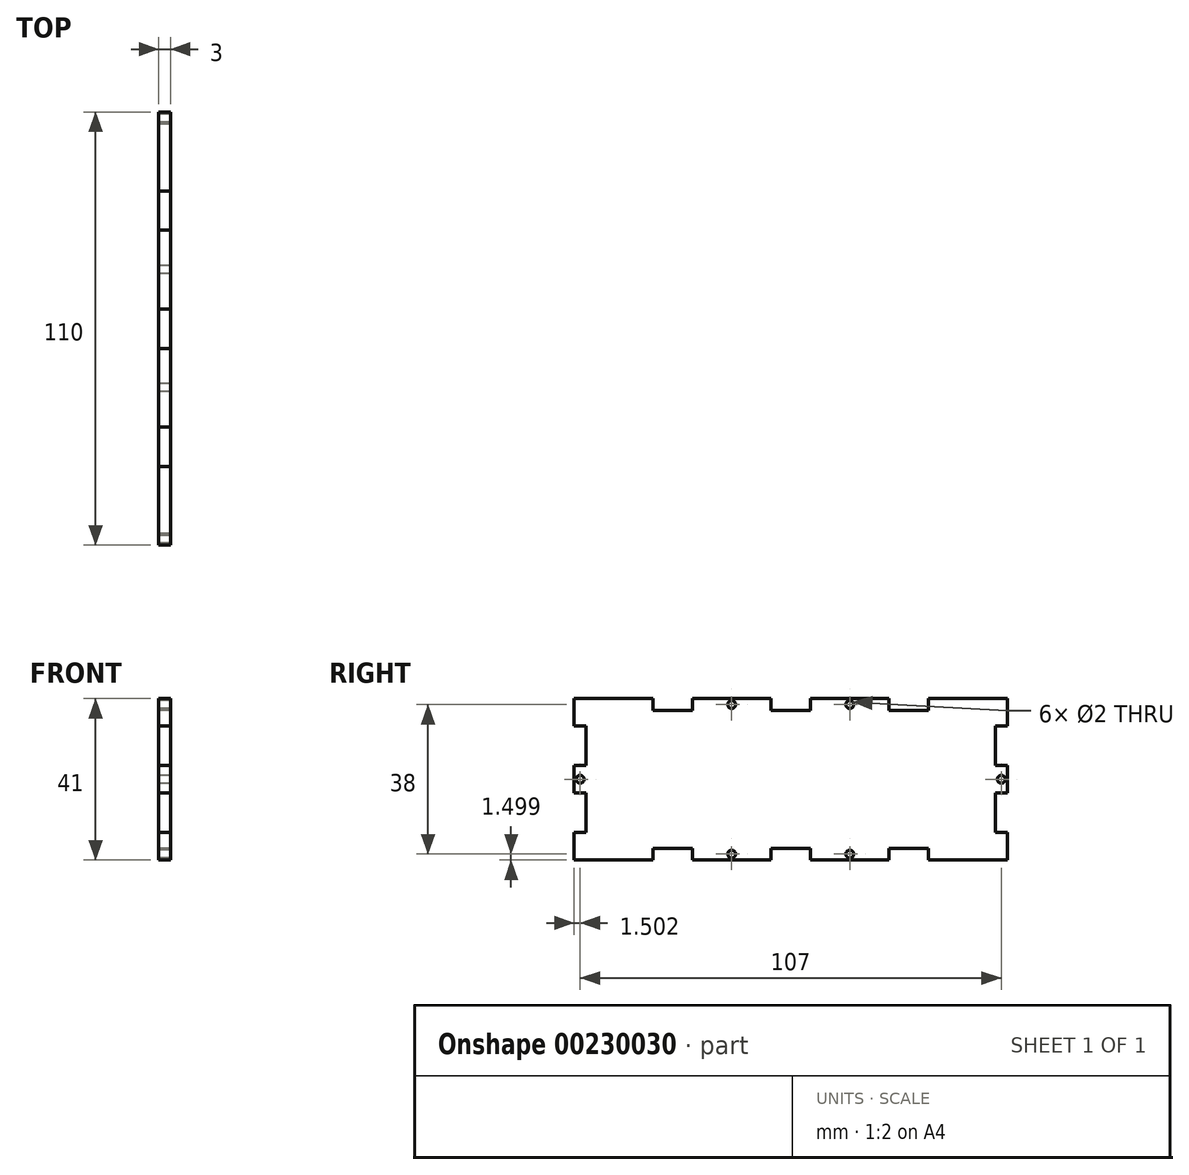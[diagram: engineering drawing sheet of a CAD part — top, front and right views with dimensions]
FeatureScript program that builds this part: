
annotation { "Feature Type Name" : "Feature", "Feature Type Description" : "" }
export const myFeature = defineFeature(function(context is Context, id is Id, definition is map)
    precondition{}
    {
        {
            var Q0;
            Q0=qCreatedBy(makeId("Right.planeOp"),FACE);
            var sketch = newSketch(context, id + "F0", { "sketchPlane" : qUnion([Q0])});
            skLineSegment(sketch, "E0", {"start": v(-98.44, -9.7) * mm, "end": v(-98.44, -2.7) * mm});
            skLineSegment(sketch, "E1", {"start": v(-98.44, -2.7) * mm, "end": v(-95.44, -2.7) * mm});
            skLineSegment(sketch, "E2", {"start": v(-95.44, -2.7) * mm, "end": v(-95.44, 7.3) * mm});
            skLineSegment(sketch, "E3", {"start": v(-95.44, 7.3) * mm, "end": v(-98.44, 7.3) * mm});
            skLineSegment(sketch, "E4", {"start": v(-98.44, 7.3) * mm, "end": v(-98.44, 14.3) * mm});
            skLineSegment(sketch, "E5", {"start": v(-98.44, 14.3) * mm, "end": v(-95.44, 14.3) * mm});
            skLineSegment(sketch, "E6", {"start": v(-95.44, 14.3) * mm, "end": v(-95.44, 24.3) * mm});
            skLineSegment(sketch, "E7", {"start": v(-95.44, 24.3) * mm, "end": v(-98.44, 24.3) * mm});
            skLineSegment(sketch, "E8", {"start": v(-98.44, 24.3) * mm, "end": v(-98.44, 31.3) * mm});
            skLineSegment(sketch, "E9", {"start": v(-98.44, 31.3) * mm, "end": v(-78.44, 31.3) * mm});
            skLineSegment(sketch, "E10", {"start": v(-78.44, 31.3) * mm, "end": v(-78.44, 28.3) * mm});
            skLineSegment(sketch, "E11", {"start": v(-78.44, 28.3) * mm, "end": v(-68.44, 28.3) * mm});
            skLineSegment(sketch, "E12", {"start": v(-68.44, 28.3) * mm, "end": v(-68.44, 31.3) * mm});
            skLineSegment(sketch, "E13", {"start": v(-68.44, 31.3) * mm, "end": v(-48.44, 31.3) * mm});
            skLineSegment(sketch, "E14", {"start": v(-48.44, 28.3) * mm, "end": v(-43.44, 28.3) * mm});
            skLineSegment(sketch, "E15", {"start": v(-48.44, 31.3) * mm, "end": v(-48.44, 28.3) * mm});
            skLineSegment(sketch, "E16", {"start": v(-43.44, 31.23) * mm, "end": v(-43.44, -9.7) * mm, "construction": true});
            skLineSegment(sketch, "E17", {"start": v(-98.44, 10.8) * mm, "end": v(-43.44, 10.8) * mm, "construction": true});
            skCircle(sketch, "E18", {"center": v(-58.44, 29.8) * mm, "radius": 1 * mm});
            skPoint(sketch, "E18.centerSnap0", {"position": v(-58.44, 31.3) * mm});
            skPoint(sketch, "E18.centerSnap1", {"position": v(-48.44, 29.8) * mm});
            skCircle(sketch, "E19", {"center": v(-96.94, 10.8) * mm, "radius": 1 * mm});
            skPoint(sketch, "E19.centerSnap0", {"position": v(-96.94, 14.3) * mm});
            skLineSegment(sketch, "E20.MirrorCS", {"start": v(-78.44, -9.7) * mm, "end": v(-78.44, -6.7) * mm});
            skLineSegment(sketch, "E21.MirrorCS", {"start": v(-48.44, -9.7) * mm, "end": v(-48.44, -6.7) * mm});
            skLineSegment(sketch, "E22.MirrorCS", {"start": v(-68.44, -6.7) * mm, "end": v(-68.44, -9.7) * mm});
            skCircle(sketch, "E23.MirrorC", {"center": v(-58.44, -8.2) * mm, "radius": 1 * mm});
            skLineSegment(sketch, "E24.MirrorCS", {"start": v(-78.44, -6.7) * mm, "end": v(-68.44, -6.7) * mm});
            skLineSegment(sketch, "E25.MirrorCS", {"start": v(-68.44, -9.7) * mm, "end": v(-48.44, -9.7) * mm});
            skPoint(sketch, "E26.MirrorP", {"position": v(-58.44, -9.7) * mm});
            skPoint(sketch, "E27.MirrorP", {"position": v(-48.44, -8.2) * mm});
            skLineSegment(sketch, "E28.MirrorCS", {"start": v(-98.44, -9.7) * mm, "end": v(-78.44, -9.7) * mm});
            skLineSegment(sketch, "E29.MirrorCS", {"start": v(-48.44, -6.7) * mm, "end": v(-43.44, -6.7) * mm});
            skLineSegment(sketch, "E30.MirrorCS", {"start": v(-38.44, 31.3) * mm, "end": v(-38.44, 28.3) * mm});
            skLineSegment(sketch, "E31.MirrorCS", {"start": v(8.56, 24.3) * mm, "end": v(11.56, 24.3) * mm});
            skLineSegment(sketch, "E32.MirrorCS", {"start": v(11.56, 14.3) * mm, "end": v(8.56, 14.3) * mm});
            skLineSegment(sketch, "E33.MirrorCS", {"start": v(11.56, -2.7) * mm, "end": v(8.56, -2.7) * mm});
            skLineSegment(sketch, "E34.MirrorCS", {"start": v(8.56, 7.3) * mm, "end": v(11.56, 7.3) * mm});
            skLineSegment(sketch, "E35.MirrorCS", {"start": v(-8.44, 31.3) * mm, "end": v(-8.44, 28.3) * mm});
            skLineSegment(sketch, "E36.MirrorCS", {"start": v(-18.44, 28.3) * mm, "end": v(-18.44, 31.3) * mm});
            skLineSegment(sketch, "E37.MirrorCS", {"start": v(-38.44, -9.7) * mm, "end": v(-38.44, -6.7) * mm});
            skCircle(sketch, "E38.MirrorC", {"center": v(10.06, 10.8) * mm, "radius": 1 * mm});
            skCircle(sketch, "E39.MirrorC", {"center": v(-28.44, -8.2) * mm, "radius": 1 * mm});
            skCircle(sketch, "E40.MirrorC", {"center": v(-28.44, 29.8) * mm, "radius": 1 * mm});
            skLineSegment(sketch, "E41.MirrorCS", {"start": v(11.56, 7.3) * mm, "end": v(11.56, 14.3) * mm});
            skLineSegment(sketch, "E42.MirrorCS", {"start": v(-18.44, 31.3) * mm, "end": v(-38.44, 31.3) * mm});
            skPoint(sketch, "E43.MirrorP", {"position": v(10.06, 14.3) * mm});
            skLineSegment(sketch, "E44.MirrorCS", {"start": v(-8.44, -6.7) * mm, "end": v(-18.44, -6.7) * mm});
            skLineSegment(sketch, "E45.MirrorCS", {"start": v(11.56, -9.7) * mm, "end": v(-8.44, -9.7) * mm});
            skPoint(sketch, "E46.MirrorP", {"position": v(-28.44, 31.3) * mm});
            skLineSegment(sketch, "E47.MirrorCS", {"start": v(8.56, 14.3) * mm, "end": v(8.56, 24.3) * mm});
            skPoint(sketch, "E48.MirrorP", {"position": v(-38.44, 29.8) * mm});
            skLineSegment(sketch, "E49.MirrorCS", {"start": v(11.56, -9.7) * mm, "end": v(11.56, -2.7) * mm});
            skPoint(sketch, "E50.MirrorP", {"position": v(-28.44, -9.7) * mm});
            skLineSegment(sketch, "E51.MirrorCS", {"start": v(11.56, 24.3) * mm, "end": v(11.56, 31.3) * mm});
            skLineSegment(sketch, "E52.MirrorCS", {"start": v(8.56, -2.7) * mm, "end": v(8.56, 7.3) * mm});
            skLineSegment(sketch, "E53.MirrorCS", {"start": v(11.56, 31.3) * mm, "end": v(-8.44, 31.3) * mm});
            skLineSegment(sketch, "E54.MirrorCS", {"start": v(-8.44, 28.3) * mm, "end": v(-18.44, 28.3) * mm});
            skLineSegment(sketch, "E55.MirrorCS", {"start": v(-18.44, -9.7) * mm, "end": v(-38.44, -9.7) * mm});
            skLineSegment(sketch, "E56.MirrorCS", {"start": v(-18.44, -6.7) * mm, "end": v(-18.44, -9.7) * mm});
            skLineSegment(sketch, "E57.MirrorCS", {"start": v(-8.44, -9.7) * mm, "end": v(-8.44, -6.7) * mm});
            skPoint(sketch, "E58.MirrorP", {"position": v(-38.44, -8.2) * mm});
            skLineSegment(sketch, "E59.MirrorCS", {"start": v(-38.44, -6.7) * mm, "end": v(-43.44, -6.7) * mm});
            skLineSegment(sketch, "E60.MirrorCS", {"start": v(-38.44, 28.3) * mm, "end": v(-43.44, 28.3) * mm});
            skPoint(sketch, "E61.centerSnap0", {"position": v(11.56, 10.8) * mm});
            skPoint(sketch, "E62.centerSnap0", {"position": v(-95.44, 19.3) * mm});
            skPoint(sketch, "E62.centerSnap1", {"position": v(-73.44, 28.3) * mm});
            skPoint(sketch, "E63.centerSnap0", {"position": v(-95.44, 2.3) * mm});
            skPoint(sketch, "E63.centerSnap1", {"position": v(-73.44, -6.7) * mm});
            skSolve(sketch);
        }
        {
            var Q0;
            Q0 = qSketchRegion(id + "F0", true);
            extrude(context, id + "F1", {"entities" : qUnion([Q0]), "depth" : 3 * mm});
        }
    });
